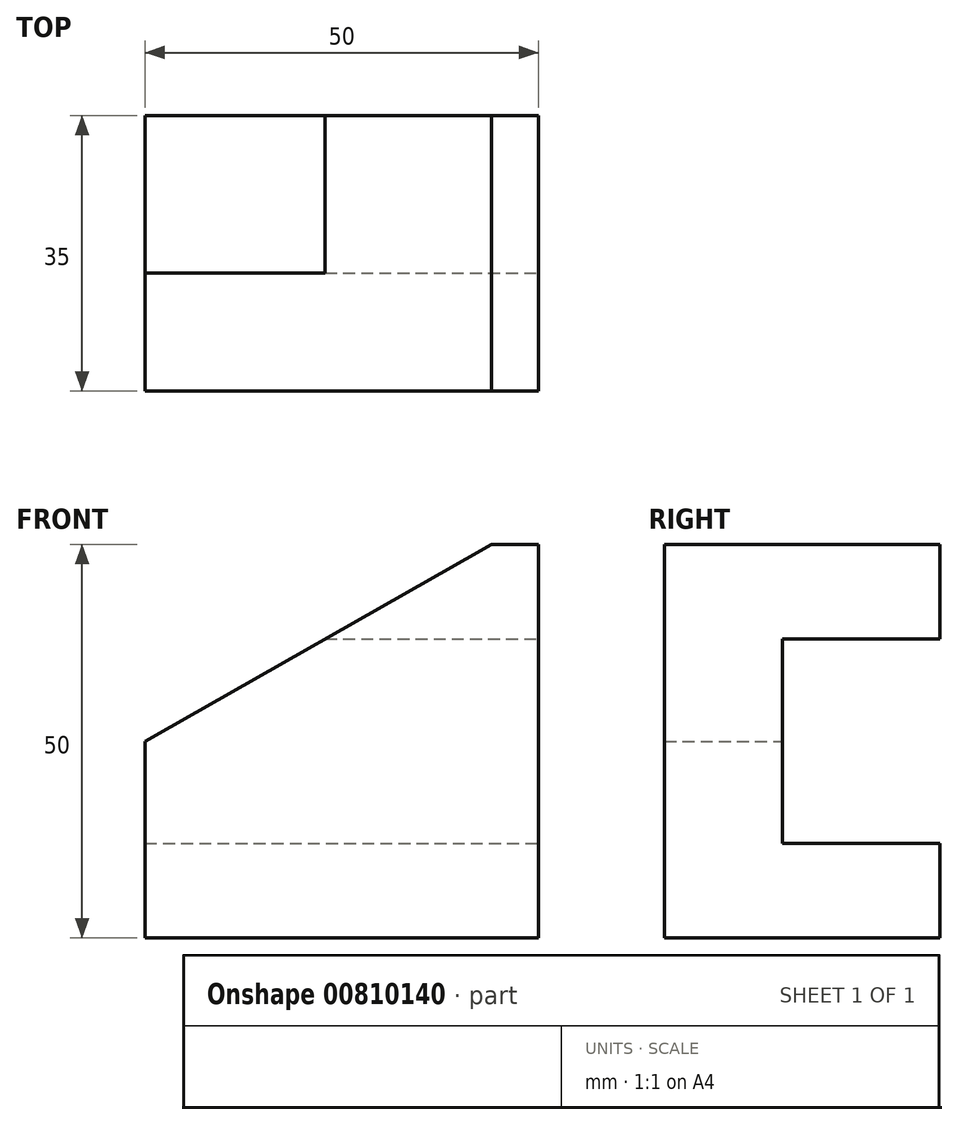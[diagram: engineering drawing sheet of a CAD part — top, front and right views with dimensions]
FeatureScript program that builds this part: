
annotation { "Feature Type Name" : "Feature", "Feature Type Description" : "" }
export const myFeature = defineFeature(function(context is Context, id is Id, definition is map)
    precondition{}
    {
        {
            var Q0;
            Q0=qCreatedBy(makeId("Front.planeOp"),FACE);
            var sketch = newSketch(context, id + "F0", { "sketchPlane" : qUnion([Q0])});
            skLineSegment(sketch, "E0", {"start": v(0, 0) * mm, "end": v(-50, 0) * mm});
            skLineSegment(sketch, "E1", {"start": v(-50, 0) * mm, "end": v(-50, 25) * mm});
            skLineSegment(sketch, "E2", {"start": v(0, 0) * mm, "end": v(0, 50) * mm});
            skLineSegment(sketch, "E3", {"start": v(0, 50) * mm, "end": v(-6, 50) * mm});
            skLineSegment(sketch, "E4", {"start": v(-6, 50) * mm, "end": v(-50, 25) * mm});
            skSolve(sketch);
        }
        {
            var Q0;
            Q0 = qSketchRegion(id + "F0", true);
            var Q1;
            Q1=makeQuery(id+"F0.imprint","IMPRINT",FACE,{"disambiguationData":[TD([[makeQuery(id+"F0.imprint","IMPRINT",EDGE,{"derivedFrom":sQuery(id+"F0.wireOp",EDGE,"E0")}),-1.0]])]});
            extrude(context, id + "F1", {"entities" : qUnion([Q0, Q1]), "depth" : 35 * mm, "offsetDistance" : 25 * mm});
        }
        {
            var Q0;
            Q0=qCreatedBy(makeId("Front.planeOp"),FACE);
            var sketch = newSketch(context, id + "F2", { "sketchPlane" : qUnion([Q0])});
            skLineSegment(sketch, "E5.bottom", {"start": v(-50, 12) * mm, "end": v(0, 12) * mm});
            skLineSegment(sketch, "E5.top", {"start": v(-50, 38) * mm, "end": v(0, 38) * mm});
            skLineSegment(sketch, "E5.left", {"start": v(-50, 12) * mm, "end": v(-50, 38) * mm});
            skLineSegment(sketch, "E5.right", {"start": v(0, 12) * mm, "end": v(0, 38) * mm});
            skSolve(sketch);
        }
        {
            var Q0;
            Q0 = qSketchRegion(id + "F2", true);
            extrude(context, id + "F3", {"entities" : qUnion([Q0]), "operationType" : NewBodyOperationType.REMOVE, "depth" : 20 * mm, "offsetDistance" : 25 * mm});
        }
    });
